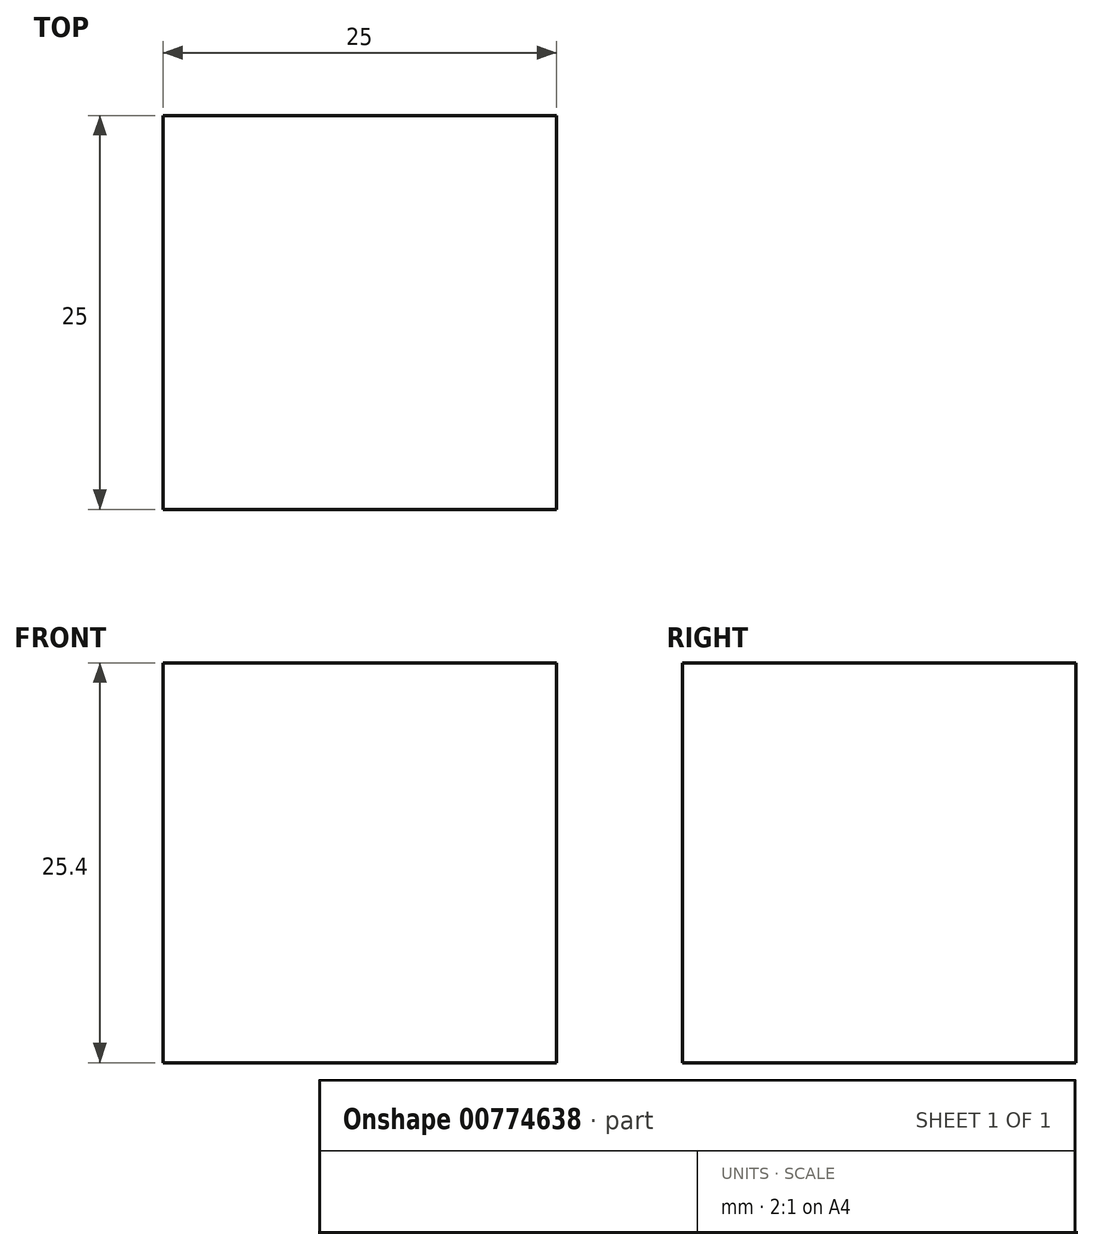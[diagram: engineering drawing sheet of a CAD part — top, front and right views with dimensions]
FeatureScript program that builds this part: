
annotation { "Feature Type Name" : "Feature", "Feature Type Description" : "" }
export const myFeature = defineFeature(function(context is Context, id is Id, definition is map)
    precondition{}
    {
        {
            var Q0;
            Q0=qCreatedBy(makeId("Top.planeOp"),FACE);
            var sketch = newSketch(context, id + "F0", { "sketchPlane" : qUnion([Q0])});
            skLineSegment(sketch, "E0.bottom", {"start": v(12.5, -12.5) * mm, "end": v(-12.5, -12.5) * mm});
            skLineSegment(sketch, "E0.top", {"start": v(12.5, 12.5) * mm, "end": v(-12.5, 12.5) * mm});
            skLineSegment(sketch, "E0.left", {"start": v(12.5, -12.5) * mm, "end": v(12.5, 12.5) * mm});
            skLineSegment(sketch, "E0.right", {"start": v(-12.5, -12.5) * mm, "end": v(-12.5, 12.5) * mm});
            skPoint(sketch, "E0.middle", {"position": v(0, 0) * mm});
            skSolve(sketch);
        }
        {
            var Q0;
            Q0=makeQuery(id+"F0.imprint","IMPRINT",FACE,{"disambiguationData":[TD([[makeQuery(id+"F0.imprint","IMPRINT",EDGE,{"derivedFrom":sQuery(id+"F0.wireOp",EDGE,"E0.bottom")}),-1.0]])]});
            extrude(context, id + "F1", {"entities" : qUnion([Q0]), "depth" : 25.4 * mm, "offsetDistance" : 25.4 * mm});
        }
        {
            var Q0;
            Q0=makeQuery(id+"F1.opExtrude","CAP_FACE",FACE,{"disambiguationData":[OSD([sQuery(id+"F0.wireOp",EDGE,"E0.bottom"),sQuery(id+"F0.wireOp",EDGE,"E0.top"),sQuery(id+"F0.wireOp",EDGE,"E0.left"),sQuery(id+"F0.wireOp",EDGE,"E0.right")])],"isStart":true});
            var sketch = newSketch(context, id + "F2", { "sketchPlane" : qUnion([Q0])});
            skCircle(sketch, "E1", {"center": v(5.62, 5.7) * mm, "radius": 4.52 * mm});
            skSolve(sketch);
        }
        {
            var Q0;
            Q0=sQuery(id+"F2.wireOp",EDGE,"E1");
            extrude(context, id + "F3", {"bodyType" : ToolBodyType.SURFACE, "surfaceEntities" : qUnion([Q0]), "depth" : 4 * mm, "offsetDistance" : 25 * mm});
        }
        {
            var Q0;
            Q0 = qSketchRegion(id + "F0", true);
            extrude(context, id + "F4", {"entities" : qUnion([Q0]), "operationType" : NewBodyOperationType.ADD, "depth" : 25 * mm, "offsetDistance" : 25 * mm});
        }
    });
